# Revit family: Door_Aluminum_PGT_SGD730-2Panel-Corner
name_source: partatom
category: Doors
revit_build: Autodesk Revit 2018 (Build: 20170927_1515(x64)
units: mm (PartAtom-declared; Revit-internal decimal feet)

## family parameters
Always vertical = Yes
Cut with Voids When Loaded = No
Host = Wall
OmniClass Number = <OmniClass>
Room Calculation Point = No
Shared = No

## types (1)
- type 2
    Air Space Below Door = 0' - 1 1/8"
    Assembly Code = B2030100
    Description = PGT Hurricane Window as Specified
    Door Frame Finish = <By Category>
    Door Frame Material = Metal - Aluminum - PGT - Anodized - Bronze
    Door Slab Finish = <By Category>
    Door Slab Material = Metal - Aluminum - PGT - Anodized - Bronze
    Expected Lifespan (Years) = 0
    Fire Rating = As Specified
    Frame Thickness = 0' - 4 1/4"
    Function = Interior
    Glass Type = Glass - Clear - PGT
    Glazing Thickness = 0' - 1"
    Hardware Finish = Metal - Stainless Steel - PGT - Brushed
    Height = 6' - 8"
    Jamb Thickness_Sides = 0' - 0"
    Jamb Thickness_Top = 0' - 0"
    Keynote = 08589
    Maintenance Schedule (Months) = 0
    Manufacturer = PGT Industries
    Manufacturer Fax = 941-486-8369
    Manufacturer Website = http://www.pgtindustries.com
    Model = As Specified in 08589
    Muntins Horizontal = 5
    Muntins Vertical = 2
    Panel Height = 6' - 5 3/8"
    Panel Width = 3' - 0 1/4"
    Product Data = http://www.arcat.com
    R-Value = 0
    RO Spacing Sides = 0' - 0 1/2"
    RO Spacing Top = 0' - 0 1/2"
    Rough Height = 6' - 8 1/2"
    Rough Width = 6' - 1"
    Sales Information = http://www.pgtindustries.com
    Screen Height = 6' - 6 3/4"
    Send Message = http://www.arcat.com
    Thickness = 0' - 1 3/4"
    URL = http://www.pgtindustries.com
    Wall Closure = By host
    Warranty Duration (Years) = 0
    Width = 6' - 0"
    new thickness = 0' - 1 3/4"

## geometry (parser evidence)
native form markers: Blend x26, Sweep x7
no freeform markers — native parametric forms only
